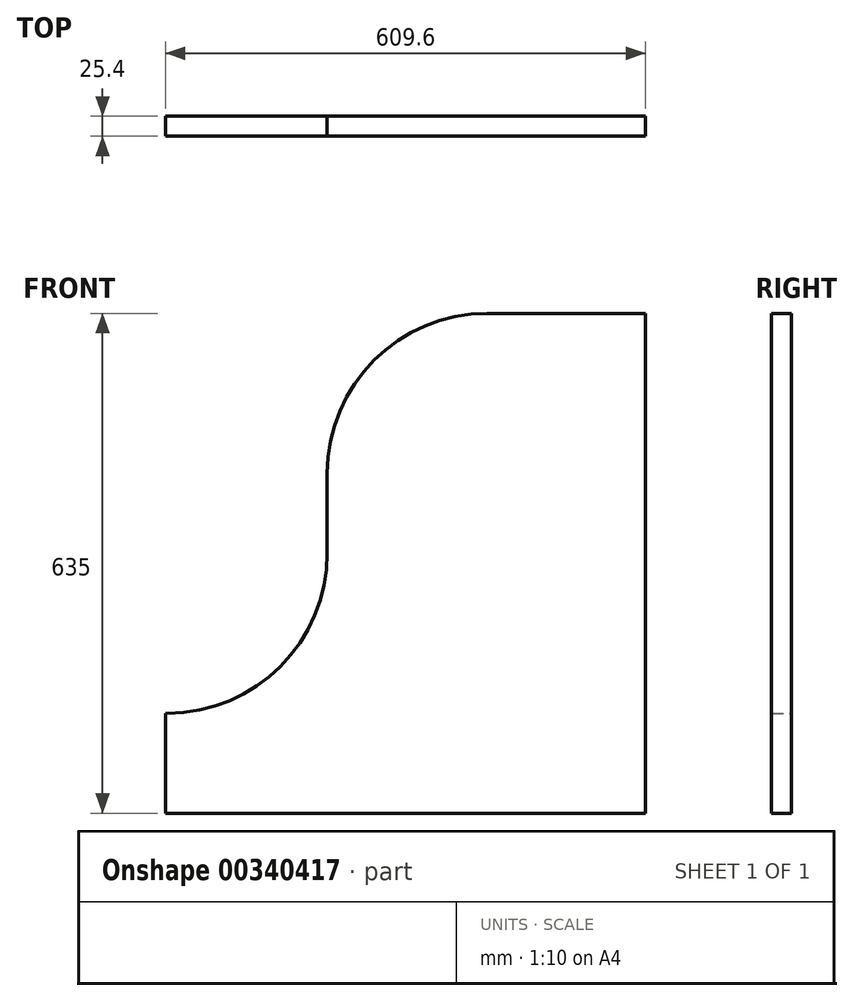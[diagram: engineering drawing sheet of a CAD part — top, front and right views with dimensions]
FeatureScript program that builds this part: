
annotation { "Feature Type Name" : "Feature", "Feature Type Description" : "" }
export const myFeature = defineFeature(function(context is Context, id is Id, definition is map)
    precondition{}
    {
        {
            var Q0;
            Q0=qCreatedBy(makeId("Front.planeOp"),FACE);
            var sketch = newSketch(context, id + "F0", { "sketchPlane" : qUnion([Q0])});
            skLineSegment(sketch, "E0.bottom", {"start": v(277.23, 86.5) * mm, "end": v(404.23, 86.5) * mm});
            skLineSegment(sketch, "E0.top", {"start": v(-205.37, -548.5) * mm, "end": v(404.23, -548.5) * mm});
            skLineSegment(sketch, "E0.left", {"start": v(-205.37, -421.5) * mm, "end": v(-205.37, -548.5) * mm});
            skLineSegment(sketch, "E0.right", {"start": v(404.23, 86.5) * mm, "end": v(404.23, -548.5) * mm});
            skPoint(sketch, "E1.newPointA", {"position": v(0, -176.9) * mm});
            skPoint(sketch, "E2.visualSharp", {"position": v(0, 0) * mm});
            skLineSegment(sketch, "E3", {"start": v(0, -116.7) * mm, "end": v(0, -176.9) * mm});
            skLineSegment(sketch, "E4", {"start": v(-205.37, -421.5) * mm, "end": v(-203.2, -421.5) * mm});
            skLineSegment(sketch, "E5", {"start": v(0, -176.9) * mm, "end": v(0, -218.3) * mm});
            skArc(sketch, "E6.filletArc", {"start": v(-203.2, -421.5) * mm, "mid": v(-59.52, -361.98) * mm, "end": v(0, -218.3) * mm});
            skLineSegment(sketch, "E7", {"start": v(277.23, 86.5) * mm, "end": v(203.2, 86.5) * mm});
            skArc(sketch, "E8.filletArc", {"start": v(203.2, 86.5) * mm, "mid": v(59.52, 27) * mm, "end": v(0, -116.7) * mm});
            skSolve(sketch);
        }
        {
            var Q0;
            Q0=makeQuery(id+"F0.imprint","IMPRINT",FACE,{"disambiguationData":[TD([[makeQuery(id+"F0.imprint","IMPRINT",EDGE,{"derivedFrom":sQuery(id+"F0.wireOp",EDGE,"E0.bottom")}),-1.0]])]});
            extrude(context, id + "F1", {"entities" : qUnion([Q0]), "depth" : 25.4 * mm});
        }
    });
